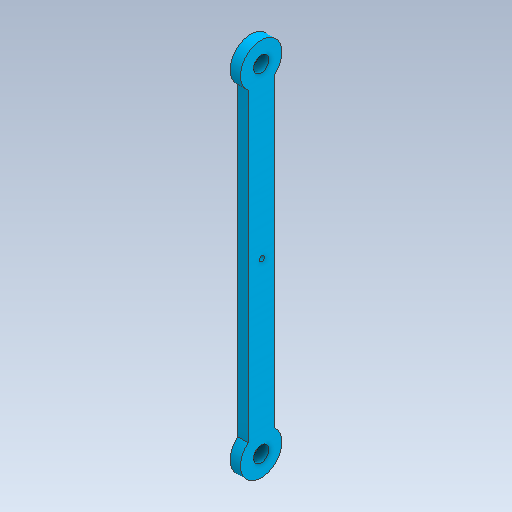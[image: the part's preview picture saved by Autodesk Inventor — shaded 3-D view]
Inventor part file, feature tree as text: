
AUTODESK INVENTOR PART (.ipt)
format: ipt  version: 2020 (Build 240168000, 168)  size: 121,344 bytes
history: native  units: in
note: dims shown in document units (in); Inventor stores cm internally (conversion verified against a paired STEP export)
features: extrude x1, sketch x1
ambient origin geometry x8: Origin, YZ Plane, XZ Plane, XY Plane, X Axis, Y Axis, Z Axis, Center Point
bodies: Solid1 (feature_tree)
feature tree (2):
  extrude  "Extrusion1"  Depth=1.9685in
  sketch  "Sketch1"  dims[d0=23.622in d1=1.9685in d2=0.9843in d3=11.811in d4=1.1811in d5=0.9843in d6=3.1496in d11=0.3937in d12=0.7874in d13=0.0in d14=0.0in d15=1.1811in d16=3.1496in d17=0.9843in]
